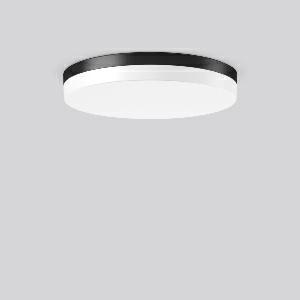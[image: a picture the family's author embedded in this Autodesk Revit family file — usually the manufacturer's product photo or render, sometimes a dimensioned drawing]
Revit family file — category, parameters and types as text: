
# Revit family: flat_slim_round_312633_0031_76_f1a1
name_source: partatom
category: Lighting Fixtures
units: mm (PartAtom-declared; Revit-internal decimal feet)

## family parameters
Cut with Voids When Loaded = No
Host = Face
Light Source = No
Part Type = Normal
Room Calculation Point = No
Round Connector Dimension = Use Diameter
Shared = No

## types (1)
- MultiLumen 1 830 (1 x LED Modul 830, 3350 lm, 3000)
    Apparent Load = 31 VA
    CIE Flux Codes = 41 71 90 86 100
    Color Rendering = 80
    Color Temperature = 3000
    Default Elevation = 1800 mm
    Height = 75 mm
    Lamp = 1 x LED Modul 830
    Lamp Light Flux = 3350 lm
    Lamp count = 1
    Length = 480 mm
    Lifetime = 50000 h
    Luminous efficacy = 108 lm/W
    Manufacturer = RZB
    ModVariant = No
    Model = 312633.0031.76
    Mounting Place = Ceiling
    Mounting Type = Surface mounted
    Number of Poles = 1
    OnlyDefault = Yes
    Power Factor = 1
    Product Name = FLAT SLIM round
    Product group = Surface mounted ceiling and wall luminaires
    ProductGroupID = 305
    Protection Class = Protection class I
    Protection Degree = Degree of protection
    RLX_Detail_Level = 1
    RLX_Emergency_Light_Flux = 0 lm
    RLX_Emergency_Type = 0
    RLX_Emergency_Type_DB = No
    RlxData = <blob elided: 22861 chars, md5=14cb86a8>
    Socket = socket
    Standby Power = 0 W
    System Light Flux = 3350 lm
    System Power = 31 W
    Type Comments = MultiLumen 1 830
    Type Image = 312633.0031.jpg
    URL = http://relux.com
    VarID = multilumen_1_830
    Voltage = 0 V
    Weight = 0.00 kg
    Width = 0 mm  [stored 0 ft]

note: [stored X ft] marks values corroborated as IEEE doubles in the binary element streams (Revit-internal decimal feet)

## geometry (parser evidence)
native form markers: Blend x4, Sweep x13
no freeform markers — native parametric forms only
